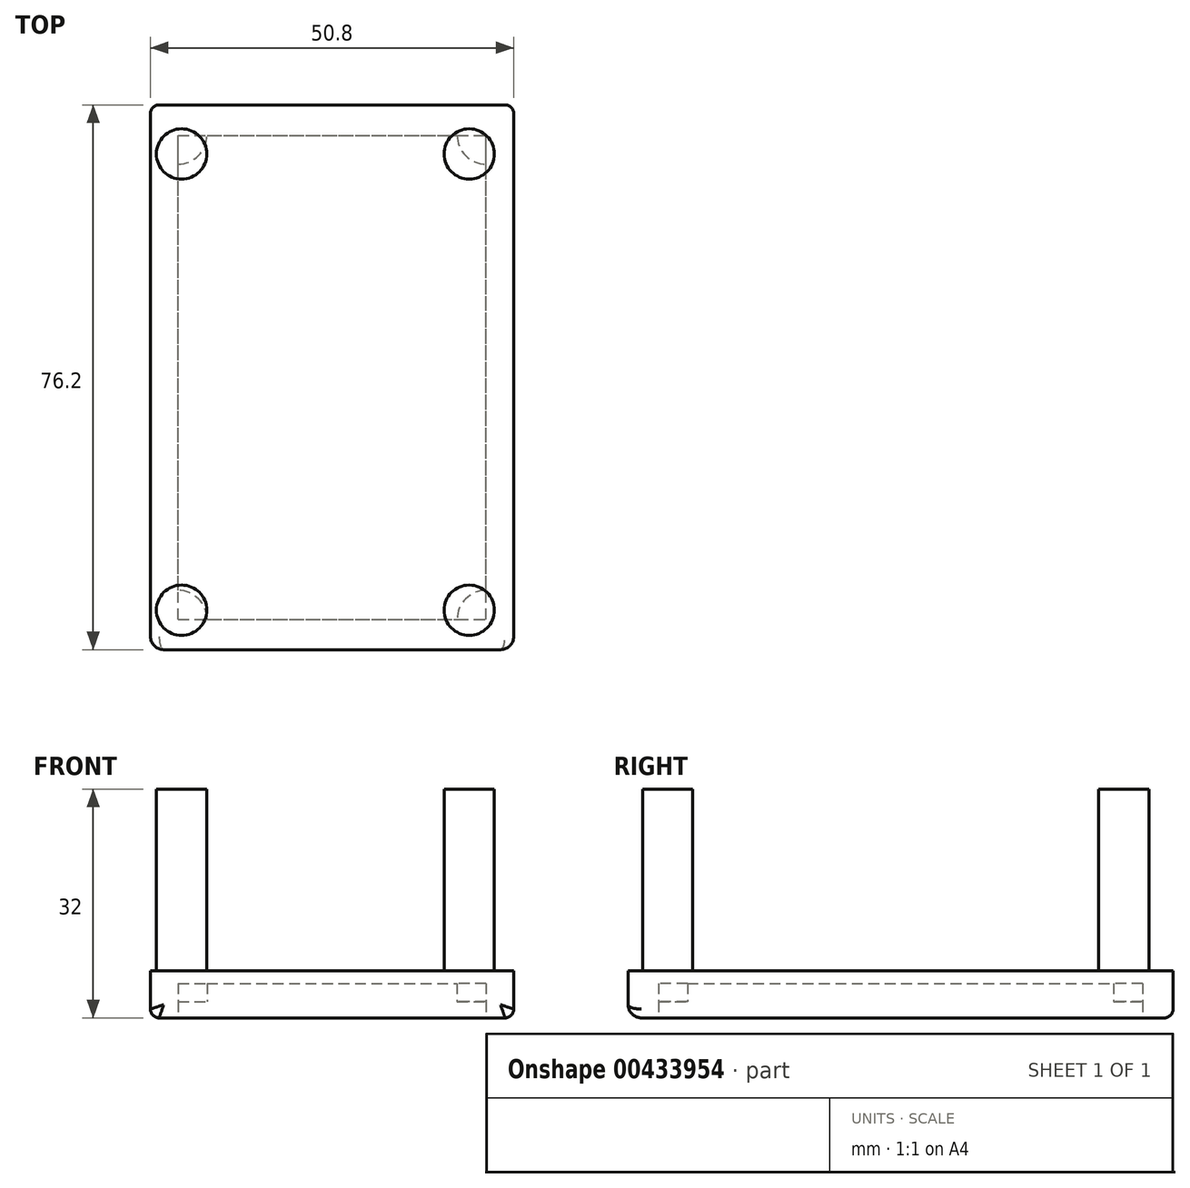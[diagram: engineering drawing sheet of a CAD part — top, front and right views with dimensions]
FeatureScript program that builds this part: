
annotation { "Feature Type Name" : "Feature", "Feature Type Description" : "" }
export const myFeature = defineFeature(function(context is Context, id is Id, definition is map)
    precondition{}
    {
        {
            var Q0;
            Q0=qCreatedBy(makeId("Top.planeOp"),FACE);
            var sketch = newSketch(context, id + "F0", { "sketchPlane" : qUnion([Q0])});
            skLineSegment(sketch, "E0.bottom", {"start": v(25.4, 38.1) * mm, "end": v(-25.4, 38.1) * mm});
            skLineSegment(sketch, "E0.top", {"start": v(25.4, -38.1) * mm, "end": v(-25.4, -38.1) * mm});
            skLineSegment(sketch, "E0.left", {"start": v(25.4, 38.1) * mm, "end": v(25.4, -38.1) * mm});
            skLineSegment(sketch, "E0.right", {"start": v(-25.4, 38.1) * mm, "end": v(-25.4, -38.1) * mm});
            skPoint(sketch, "E0.middle", {"position": v(0, 0) * mm});
            skSolve(sketch);
        }
        {
            var Q0;
            Q0=makeQuery(id+"F0.imprint","IMPRINT",FACE,{"disambiguationData":[TD([[makeQuery(id+"F0.imprint","IMPRINT",EDGE,{"derivedFrom":sQuery(id+"F0.wireOp",EDGE,"E0.bottom")}),1.0]])]});
            extrude(context, id + "F1", {"entities" : qUnion([Q0]), "depth" : 6.6 * mm});
        }
        {
            var Q0;
            Q0=makeQuery(id+"F1.opExtrude","CAP_FACE",FACE,{"disambiguationData":[OSD([sQuery(id+"F0.wireOp",EDGE,"E0.bottom"),sQuery(id+"F0.wireOp",EDGE,"E0.top"),sQuery(id+"F0.wireOp",EDGE,"E0.left"),sQuery(id+"F0.wireOp",EDGE,"E0.right")])],"isStart":false});
            var sketch = newSketch(context, id + "F2", { "sketchPlane" : qUnion([Q0])});
            skCircle(sketch, "E1", {"center": v(-21.04, 31.23) * mm, "radius": 3.52 * mm});
            skCircle(sketch, "E2", {"center": v(19.18, 31.23) * mm, "radius": 3.52 * mm});
            skCircle(sketch, "E3", {"center": v(19.18, -32.58) * mm, "radius": 3.52 * mm});
            skCircle(sketch, "E4", {"center": v(-21.04, -32.58) * mm, "radius": 3.52 * mm});
            skSolve(sketch);
        }
        {
            var Q0;
            Q0 = qSketchRegion(id + "F2", true);
            extrude(context, id + "F3", {"entities" : qUnion([Q0]), "operationType" : NewBodyOperationType.ADD, "depth" : 25.4 * mm});
        }
        {
            var Q0;
            Q0=makeQuery(id+"F1.opExtrude","CAP_EDGE",EDGE,{"disambiguationData":[OSD([sQuery(id+"F0.wireOp",EDGE,"E0.right")])],"isStart":true});
            fillet(context, id + "F4", {"entities" : qUnion([Q0]), "radius" : 1.23 * mm, "tangentPropagation" : true, "allowEdgeOverflow" : false});
        }
        {
            var Q0;
            Q0=makeQuery(id+"F1.opExtrude","CAP_EDGE",EDGE,{"disambiguationData":[OSD([sQuery(id+"F0.wireOp",EDGE,"E0.left")])],"isStart":true});
            fillet(context, id + "F5", {"entities" : qUnion([Q0]), "radius" : 1.23 * mm, "tangentPropagation" : true, "allowEdgeOverflow" : false});
        }
        {
            var Q0;
            Q0=makeQuery(id+"F1.opExtrude","CAP_EDGE",EDGE,{"disambiguationData":[OSD([sQuery(id+"F0.wireOp",EDGE,"E0.bottom")])],"isStart":true});
            fillet(context, id + "F6", {"entities" : qUnion([Q0]), "radius" : 1.23 * mm, "tangentPropagation" : true, "allowEdgeOverflow" : false});
        }
        {
            var Q0;
            Q0=makeQuery(id+"F1.opExtrude","CAP_EDGE",EDGE,{"disambiguationData":[OSD([sQuery(id+"F0.wireOp",EDGE,"E0.top")])],"isStart":true});
            fillet(context, id + "F7", {"entities" : qUnion([Q0]), "radius" : 1.84 * mm, "tangentPropagation" : true, "allowEdgeOverflow" : false});
        }
        {
            var Q0;
            Q0=makeQuery(id+"F1.opExtrude","CAP_FACE",FACE,{"disambiguationData":[OSD([sQuery(id+"F0.wireOp",EDGE,"E0.bottom"),sQuery(id+"F0.wireOp",EDGE,"E0.top"),sQuery(id+"F0.wireOp",EDGE,"E0.left"),sQuery(id+"F0.wireOp",EDGE,"E0.right")])],"isStart":true});
            var sketch = newSketch(context, id + "F8", { "sketchPlane" : qUnion([Q0])});
            skLineSegment(sketch, "E5.bottom", {"start": v(-21.53, 33.85) * mm, "end": v(21.53, 33.85) * mm});
            skLineSegment(sketch, "E5.top", {"start": v(-21.53, -33.85) * mm, "end": v(21.53, -33.85) * mm});
            skLineSegment(sketch, "E5.left", {"start": v(-21.53, 33.85) * mm, "end": v(-21.53, -33.85) * mm});
            skLineSegment(sketch, "E5.right", {"start": v(21.53, 33.85) * mm, "end": v(21.53, -33.85) * mm});
            skPoint(sketch, "E5.middle", {"position": v(0, 0) * mm});
            skSolve(sketch);
        }
        {
            var Q0;
            Q0 = qSketchRegion(id + "F8", true);
            extrude(context, id + "F9", {"entities" : qUnion([Q0]), "operationType" : NewBodyOperationType.REMOVE, "oppositeDirection" : true, "depth" : 2.3 * mm});
        }
        {
            var Q0;
            Q0=makeQuery(id+"F9.boolean.opBoolean","COPY",FACE,{"derivedFrom":makeQuery(id+"F9.opExtrude","CAP_FACE",FACE,{"disambiguationData":[OSD([sQuery(id+"F8.wireOp",EDGE,"E5.bottom"),sQuery(id+"F8.wireOp",EDGE,"E5.top"),sQuery(id+"F8.wireOp",EDGE,"E5.left"),sQuery(id+"F8.wireOp",EDGE,"E5.right")])],"isStart":false})});
            var sketch = newSketch(context, id + "F10", { "sketchPlane" : qUnion([Q0])});
            skArc(sketch, "E6", {"start": v(-17.5, 33.85) * mm, "mid": v(-18.68, 31) * mm, "end": v(-21.53, 29.81) * mm});
            skArc(sketch, "E7", {"start": v(21.53, 29.81) * mm, "mid": v(18.68, 31) * mm, "end": v(17.5, 33.85) * mm});
            skArc(sketch, "E8", {"start": v(17.5, -33.85) * mm, "mid": v(18.68, -31) * mm, "end": v(21.53, -29.81) * mm});
            skArc(sketch, "E9", {"start": v(-21.53, -29.81) * mm, "mid": v(-18.68, -31) * mm, "end": v(-17.5, -33.85) * mm});
            skSolve(sketch);
        }
        {
            var Q0;
            {var subQ0=sQuery(id+"F10.wireOp",EDGE,"E6");Q0=makeQuery(id+"F10.imprint","IMPRINT",FACE,{"disambiguationData":[TD([[makeQuery(id+"F10.imprint","IMPRINT",EDGE,{"derivedFrom":subQ0}),-1.0]])]});}
            extrude(context, id + "F11", {"entities" : qUnion([Q0]), "operationType" : NewBodyOperationType.REMOVE, "oppositeDirection" : true, "depth" : 2.54 * mm});
        }
        {
            var Q0;
            {var subQ0=sQuery(id+"F10.wireOp",EDGE,"E7");Q0=makeQuery(id+"F10.imprint","IMPRINT",FACE,{"disambiguationData":[TD([[makeQuery(id+"F10.imprint","IMPRINT",EDGE,{"derivedFrom":subQ0}),-1.0]])]});}
            var Q1;
            Q1=sQuery(id+"F10.wireOp",EDGE,"E7");
            extrude(context, id + "F12", {"entities" : qUnion([Q0]), "operationType" : NewBodyOperationType.REMOVE, "surfaceEntities" : qUnion([Q1]), "oppositeDirection" : true, "depth" : 2.54 * mm});
        }
        {
            var Q0;
            {var subQ0=sQuery(id+"F10.wireOp",EDGE,"E9");Q0=makeQuery(id+"F10.imprint","IMPRINT",FACE,{"disambiguationData":[TD([[makeQuery(id+"F10.imprint","IMPRINT",EDGE,{"derivedFrom":subQ0}),-1.0]])]});}
            extrude(context, id + "F13", {"entities" : qUnion([Q0]), "operationType" : NewBodyOperationType.REMOVE, "oppositeDirection" : true, "depth" : 2.54 * mm});
        }
        {
            var Q0;
            {var subQ0=sQuery(id+"F10.wireOp",EDGE,"E8");Q0=makeQuery(id+"F10.imprint","IMPRINT",FACE,{"disambiguationData":[TD([[makeQuery(id+"F10.imprint","IMPRINT",EDGE,{"derivedFrom":subQ0}),-1.0]])]});}
            extrude(context, id + "F14", {"entities" : qUnion([Q0]), "operationType" : NewBodyOperationType.REMOVE, "oppositeDirection" : true, "depth" : 2.54 * mm});
        }
    });
